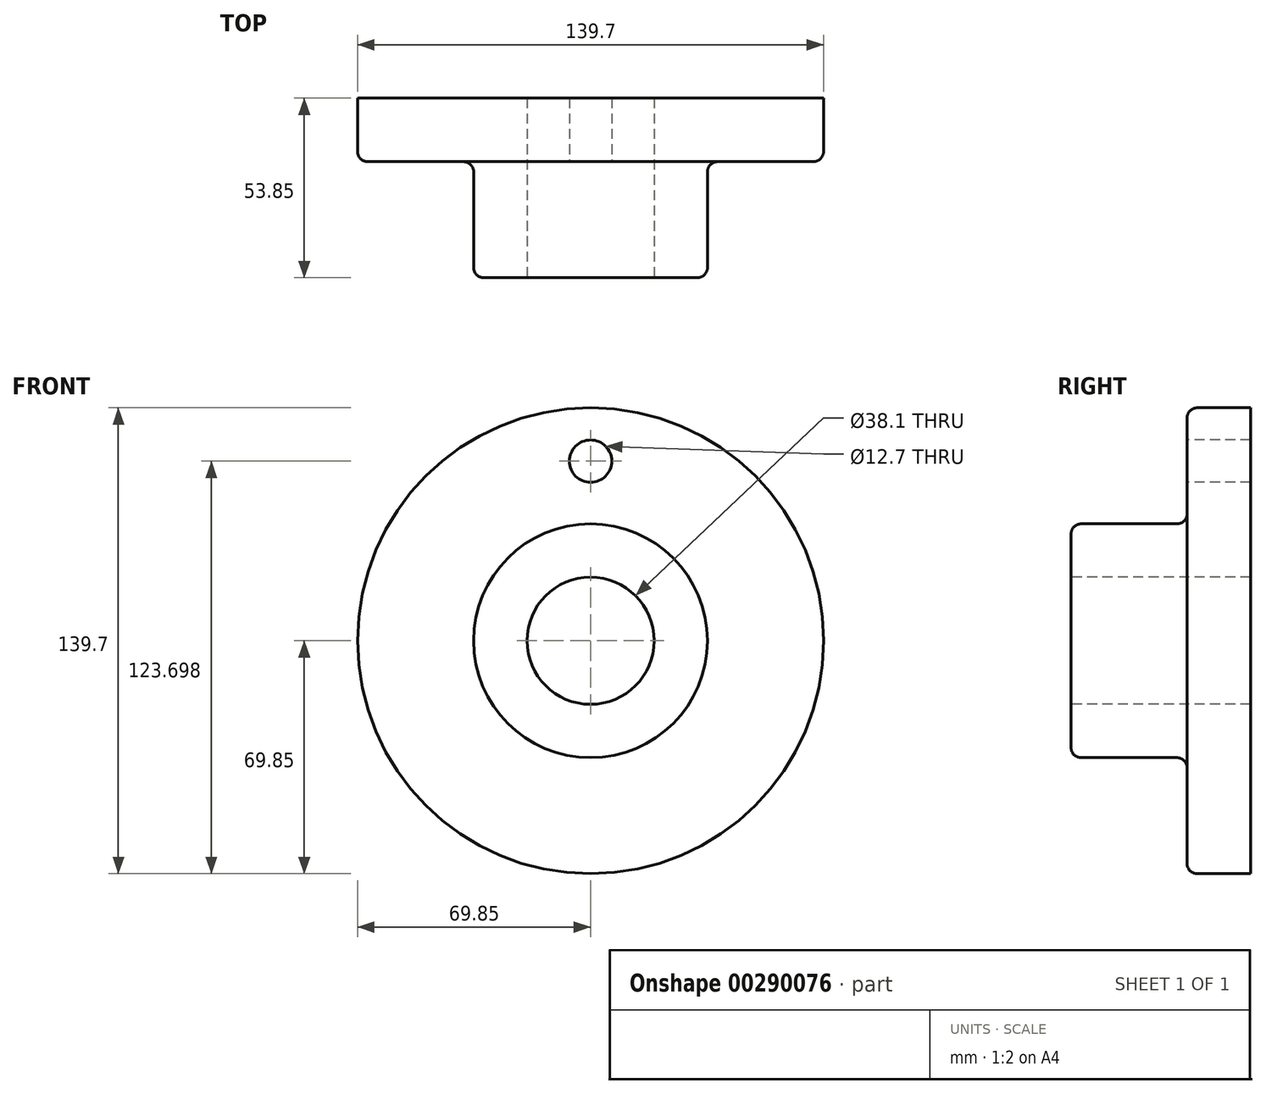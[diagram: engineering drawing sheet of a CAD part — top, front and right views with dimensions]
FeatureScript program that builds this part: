
annotation { "Feature Type Name" : "Feature", "Feature Type Description" : "" }
export const myFeature = defineFeature(function(context is Context, id is Id, definition is map)
    precondition{}
    {
        {
            var Q0;
            Q0=qCreatedBy(makeId("Right.planeOp"),FACE);
            var sketch = newSketch(context, id + "F0", { "sketchPlane" : qUnion([Q0])});
            skLineSegment(sketch, "E0", {"start": v(0, 0) * mm, "end": v(3.83, 0) * mm, "construction": true});
            skLineSegment(sketch, "E1", {"start": v(0, 0) * mm, "end": v(-1.9, 0) * mm, "construction": true});
            skLineSegment(sketch, "E2", {"start": v(0, 19.05) * mm, "end": v(53.85, 19.05) * mm});
            skLineSegment(sketch, "E3", {"start": v(53.85, 19.05) * mm, "end": v(53.85, 69.85) * mm});
            skLineSegment(sketch, "E4", {"start": v(53.85, 69.85) * mm, "end": v(34.8, 69.85) * mm});
            skLineSegment(sketch, "E5", {"start": v(34.8, 69.85) * mm, "end": v(34.8, 35.05) * mm});
            skLineSegment(sketch, "E6", {"start": v(34.8, 35.05) * mm, "end": v(0, 35.05) * mm});
            skLineSegment(sketch, "E7", {"start": v(0, 35.05) * mm, "end": v(0, 19.05) * mm});
            skSolve(sketch);
        }
        {
            var Q0;
            Q0=makeQuery(id+"F0.imprint","IMPRINT",FACE,{"disambiguationData":[TD([[makeQuery(id+"F0.imprint","IMPRINT",EDGE,{"derivedFrom":sQuery(id+"F0.wireOp",EDGE,"E2")}),1.0]])]});
            var Q1;
            Q1=sQuery(id+"F0.wireOp",EDGE,"E0");
            revolve(context, id + "F1", {"entities" : qUnion([Q0]), "axis" : qUnion([Q1]), "revolveType" : RevolveType.FULL});
        }
        {
            var Q0;
            Q0=makeQuery(id+"F1.opRevolve","SWEPT_FACE",FACE,{"disambiguationData":[OSD([sQuery(id+"F0.wireOp",EDGE,"E5")])]});
            var sketch = newSketch(context, id + "F2", { "sketchPlane" : qUnion([Q0])});
            skCircle(sketch, "E8", {"center": v(0, 53.85) * mm, "radius": 6.35 * mm});
            skCircle(sketch, "E9", {"center": v(0, 0) * mm, "radius": 53.85 * mm, "construction": true});
            skSolve(sketch);
        }
        {
            var Q0;
            Q0=makeQuery(id+"F2.imprint","IMPRINT",FACE,{"disambiguationData":[TD([[makeQuery(id+"F2.imprint","IMPRINT",EDGE,{"derivedFrom":sQuery(id+"F2.wireOp",EDGE,"E8")}),1.0]])]});
            extrude(context, id + "F3", {"entities" : qUnion([Q0]), "operationType" : NewBodyOperationType.REMOVE, "endBound" : BoundingType.THROUGH_ALL, "oppositeDirection" : true, "depth" : 25 * mm});
        }
        {
            var Q0;
            Q0=makeQuery(id+"F1.opRevolve","SWEPT_EDGE",EDGE,{"disambiguationData":[OSD([sQuery(id+"F0.wireOp",EDGE,"E4"),sQuery(id+"F0.wireOp",EDGE,"E5")])]});
            var Q1;
            Q1=makeQuery(id+"F1.opRevolve","SWEPT_EDGE",EDGE,{"disambiguationData":[OSD([sQuery(id+"F0.wireOp",EDGE,"E5"),sQuery(id+"F0.wireOp",EDGE,"E6")])]});
            var Q2;
            Q2=makeQuery(id+"F1.opRevolve","SWEPT_EDGE",EDGE,{"disambiguationData":[OSD([sQuery(id+"F0.wireOp",EDGE,"E6"),sQuery(id+"F0.wireOp",EDGE,"E7")])]});
            fillet(context, id + "F4", {"entities" : qUnion([Q0, Q1, Q2]), "radius" : 3.05 * mm, "tangentPropagation" : true, "allowEdgeOverflow" : false});
        }
    });
